# Revit family: P190780JX-028c_JJB6424HM_Urban_Living_Coffee-Maker
name_source: partatom
category: Specialty Equipment
units: mm (PartAtom-declared; Revit-internal decimal feet)

## family parameters
Always vertical = Yes
Cut with Voids When Loaded = No
Enable Cutting in Views = No
Maintain Annotation Orientation = No
Part Type = Normal
Room Calculation Point = No
Round Connector Dimension = Use Diameter
Shared = No
Work Plane-Based = No

## types (1)
- JJB6424HM
    Accent Material = ARCAT - Metal - Steel - White
    Amps = 0 A
    Body Material = ARCAT - Metal - Steel - Stainless
    Default Elevation = 0"
    Depth = 19 11/16"
    Description = JennAir® RISE™ 60cm Built-In Coffee System
JennAir® Machine à café encastrée JennAir® RISE™
    Dimension Guide = https://www.whirlpool.com
    Family Name = SMALL SPACES - 24" - Coffee Maker
    Feature 1 = BUILT-IN COFFEE SYSTEM
MACHINE À CAFÉ ENCASTRÉE
    Feature 2 = Ground Coffee Compatibility
Compatible avec du café moulu
    Feature 3 = Cup Tray with Integrated Drip Tray
Plateau à tasse avec plateau d'égouttement intégré
    Front Frame Material = ARCAT - Metal - Steel - Black
    Height = 17 7/8"
    Installation-Fabrication = https://www.whirlpool.com
    Manufacturer = JennAir
    Model = JJB6424HM
    Voltage = 0 V
    Warranty Duration (Years) = One year limited
    Width = 23 7/16"

## geometry (parser evidence)
native form markers: Sweep x4
no freeform markers — native parametric forms only
